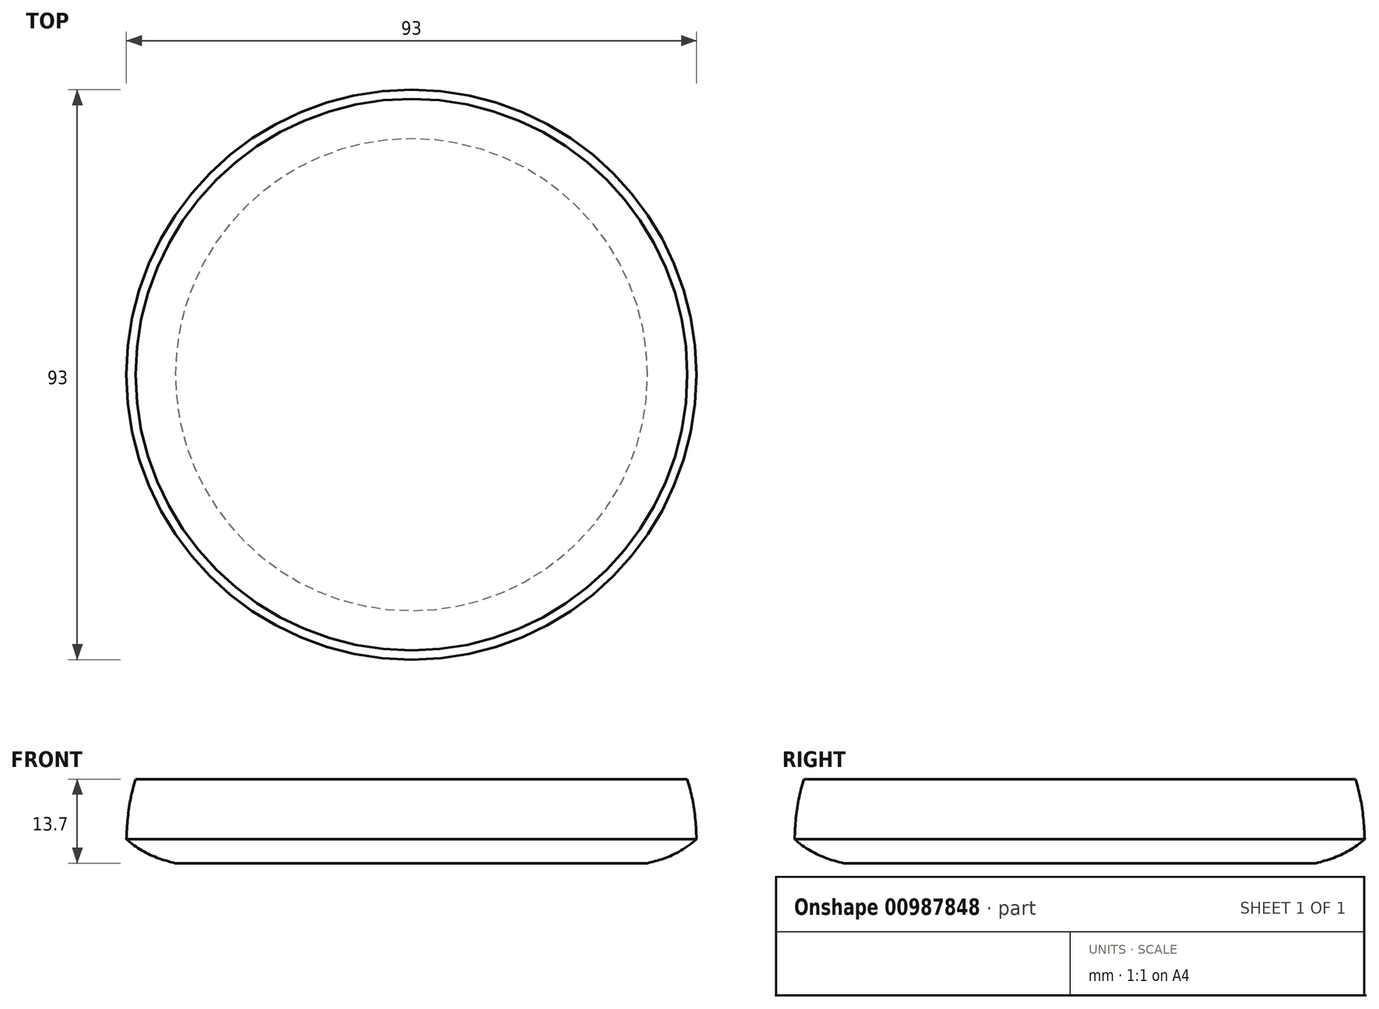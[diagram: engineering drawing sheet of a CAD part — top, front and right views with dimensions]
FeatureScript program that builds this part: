
annotation { "Feature Type Name" : "Feature", "Feature Type Description" : "" }
export const myFeature = defineFeature(function(context is Context, id is Id, definition is map)
    precondition{}
    {
        {
            var Q0;
            Q0=qCreatedBy(makeId("Front.planeOp"),FACE);
            var sketch = newSketch(context, id + "F0", { "sketchPlane" : qUnion([Q0])});
            skLineSegment(sketch, "E0", {"start": v(0, 13.7) * mm, "end": v(-45, 13.7) * mm});
            skLineSegment(sketch, "E1", {"start": v(0, 0) * mm, "end": v(-38.5, 0) * mm});
            skLineSegment(sketch, "E2", {"start": v(-46.5, 3.9) * mm, "end": v(0, 3.9) * mm, "construction": true});
            skFitSpline(sketch, "E3", {"points": [v(-45, 13.7) * mm, v(-46.5, 3.9) * mm], "startDerivative": vector(-3.07, -10.04) * mm, "endDerivative": vector(-0.4, -11.4) * mm});
            skFitSpline(sketch, "E4", {"points": [v(-46.5, 3.9) * mm, v(-38.5, 0) * mm], "startDerivative": vector(8.6, -7.48) * mm, "endDerivative": vector(7.3, -1.69) * mm});
            skLineSegment(sketch, "E5", {"start": v(0, 13.7) * mm, "end": v(0, 0) * mm});
            skLineSegment(sketch, "E6", {"start": v(-46.02, 10.35) * mm, "end": v(-45, 13.7) * mm, "construction": true});
            skLineSegment(sketch, "E7", {"start": v(-46.37, 7.7) * mm, "end": v(-46.5, 3.9) * mm, "construction": true});
            skLineSegment(sketch, "E8", {"start": v(-46.5, 3.9) * mm, "end": v(-43.63, 1.4) * mm, "construction": true});
            skLineSegment(sketch, "E9", {"start": v(-40.94, 0.56) * mm, "end": v(-38.5, 0) * mm, "construction": true});
            skSolve(sketch);
        }
        {
            var Q0;
            Q0=makeQuery(id+"F0.imprint","IMPRINT",FACE,{"disambiguationData":[TD([[makeQuery(id+"F0.imprint","IMPRINT",EDGE,{"derivedFrom":sQuery(id+"F0.wireOp",EDGE,"E0")}),1.0]])]});
            var Q1;
            Q1=sQuery(id+"F0.wireOp",EDGE,"E5");
            revolve(context, id + "F1", {"surfaceOperationType" : NewSurfaceOperationType.NEW, "entities" : qUnion([Q0]), "axis" : qUnion([Q1]), "revolveType" : RevolveType.FULL});
        }
    });
